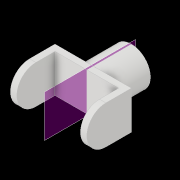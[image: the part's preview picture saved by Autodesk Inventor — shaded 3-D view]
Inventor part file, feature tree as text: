
AUTODESK INVENTOR PART (.ipt)
format: ipt  version: 2019 (Build 230136000, 136)  size: 131,584 bytes
history: native  units: mm
features: extrude x3, sketch x3, other x2, mirror x1, projected_geometry x1
ambient origin geometry x8: Origin, YZ Plane, XZ Plane, XY Plane, X Axis, Y Axis, Z Axis, Center Point
bodies: Body1 (feature_tree)
feature tree (10):
  other  "솔리드1"
  extrude  "돌출1"  Depth=30.0mm
  extrude  "돌출2"  Depth=30.0mm TaperAngle=0.0deg
  extrude  "돌출3"  Depth=60.0mm
  mirror  "미러1"
  sketch  "스케치1"
  sketch  "스케치2"
  sketch  "스케치3"
  projected_geometry  "투영된 루프1"
  other  "작업 평면1"
